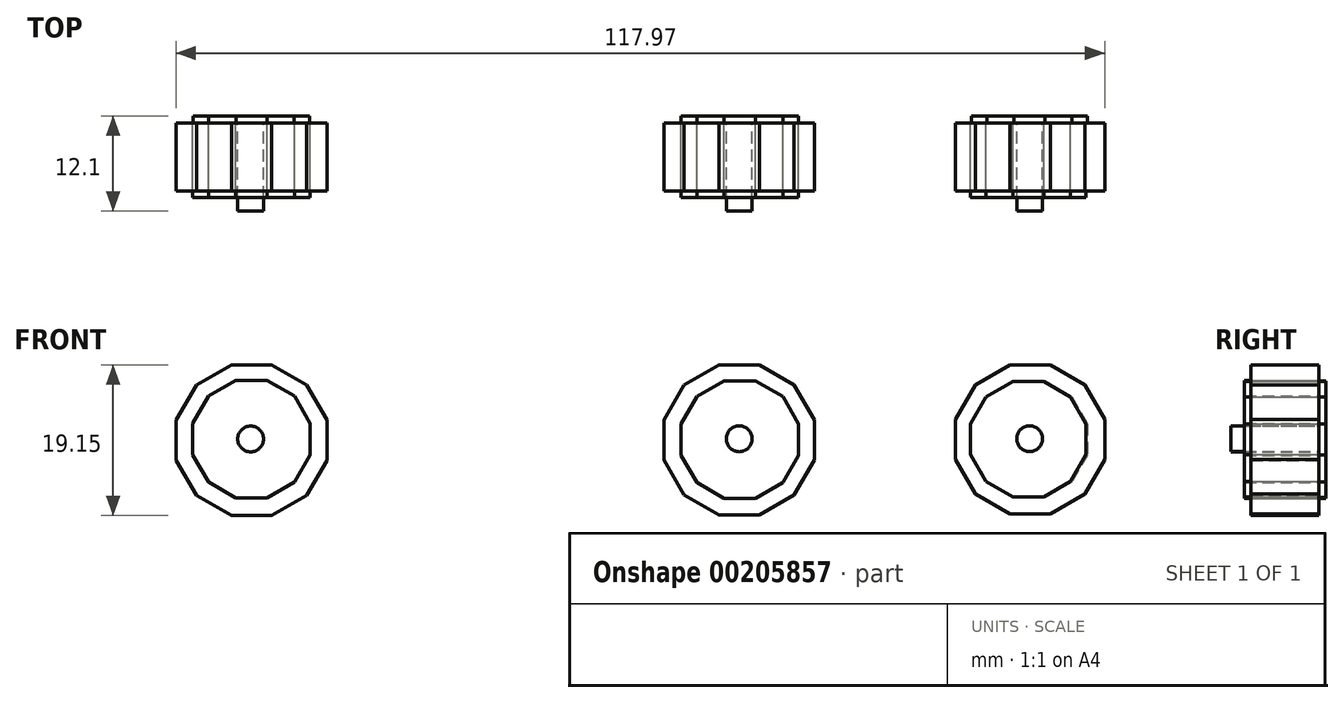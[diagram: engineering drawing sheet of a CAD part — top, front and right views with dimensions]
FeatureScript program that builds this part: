
annotation { "Feature Type Name" : "Feature", "Feature Type Description" : "" }
export const myFeature = defineFeature(function(context is Context, id is Id, definition is map)
    precondition{}
    {
        {
            var Q0;
            Q0=qCreatedBy(makeId("Front.planeOp"),FACE);
            cPlane(context, id + "F0", {"entities" : qUnion([Q0]), "cplaneType" : CPlaneType.OFFSET, "offset" : 20.32 * mm, "width" : 152.4 * mm, "height" : 152.4 * mm});
        }
        {
            var Q0;
            Q0=qCreatedBy(makeId("Front.planeOp"),FACE);
            cPlane(context, id + "F1", {"entities" : qUnion([Q0]), "cplaneType" : CPlaneType.OFFSET, "offset" : 10.16 * mm, "oppositeDirection" : true, "width" : 152.4 * mm, "height" : 152.4 * mm});
        }
        {
            var Q0;
            Q0=qCreatedBy(id+"F1.planeOp",FACE);
            var sketch = newSketch(context, id + "F2", { "sketchPlane" : qUnion([Q0])});
            skCircle(sketch, "E0.cCircle", {"center": v(54.19, -3.76) * mm, "radius": 9.48 * mm, "construction": true});
            skLineSegment(sketch, "E0.0", {"start": v(56.73, -13.25) * mm, "end": v(51.64, -13.25) * mm});
            skLineSegment(sketch, "E0.1", {"start": v(51.64, -13.25) * mm, "end": v(47.24, -10.7) * mm});
            skLineSegment(sketch, "E0.2", {"start": v(47.24, -10.7) * mm, "end": v(44.7, -6.3) * mm});
            skLineSegment(sketch, "E0.3", {"start": v(44.7, -6.3) * mm, "end": v(44.7, -1.22) * mm});
            skLineSegment(sketch, "E0.4", {"start": v(44.7, -1.22) * mm, "end": v(47.24, 3.18) * mm});
            skLineSegment(sketch, "E0.5", {"start": v(47.24, 3.18) * mm, "end": v(51.64, 5.72) * mm});
            skLineSegment(sketch, "E0.6", {"start": v(51.64, 5.72) * mm, "end": v(56.73, 5.72) * mm});
            skLineSegment(sketch, "E0.7", {"start": v(56.73, 5.72) * mm, "end": v(61.13, 3.18) * mm});
            skLineSegment(sketch, "E0.8", {"start": v(61.13, 3.18) * mm, "end": v(63.67, -1.22) * mm});
            skLineSegment(sketch, "E0.9", {"start": v(63.67, -1.22) * mm, "end": v(63.67, -6.3) * mm});
            skLineSegment(sketch, "E0.10", {"start": v(63.67, -6.3) * mm, "end": v(61.13, -10.7) * mm});
            skLineSegment(sketch, "E0.11", {"start": v(61.13, -10.7) * mm, "end": v(56.73, -13.25) * mm});
            skPoint(sketch, "E0.0.midPoint", {"position": v(54.19, -13.25) * mm});
            skCircle(sketch, "E1.cCircle", {"center": v(17.22, -3.82) * mm, "radius": 9.54 * mm, "construction": true});
            skLineSegment(sketch, "E1.0", {"start": v(14.67, 5.72) * mm, "end": v(19.78, 5.72) * mm});
            skLineSegment(sketch, "E1.1", {"start": v(19.78, 5.72) * mm, "end": v(24.21, 3.16) * mm});
            skLineSegment(sketch, "E1.2", {"start": v(24.21, 3.16) * mm, "end": v(26.77, -1.27) * mm});
            skLineSegment(sketch, "E1.3", {"start": v(26.77, -1.27) * mm, "end": v(26.77, -6.38) * mm});
            skLineSegment(sketch, "E1.4", {"start": v(26.77, -6.38) * mm, "end": v(24.21, -10.81) * mm});
            skLineSegment(sketch, "E1.5", {"start": v(24.21, -10.81) * mm, "end": v(19.78, -13.37) * mm});
            skLineSegment(sketch, "E1.6", {"start": v(19.78, -13.37) * mm, "end": v(14.67, -13.37) * mm});
            skLineSegment(sketch, "E1.7", {"start": v(14.67, -13.37) * mm, "end": v(10.24, -10.81) * mm});
            skLineSegment(sketch, "E1.8", {"start": v(10.24, -10.81) * mm, "end": v(7.68, -6.38) * mm});
            skLineSegment(sketch, "E1.9", {"start": v(7.68, -6.38) * mm, "end": v(7.68, -1.27) * mm});
            skLineSegment(sketch, "E1.10", {"start": v(7.68, -1.27) * mm, "end": v(10.24, 3.16) * mm});
            skLineSegment(sketch, "E1.11", {"start": v(10.24, 3.16) * mm, "end": v(14.67, 5.72) * mm});
            skPoint(sketch, "E1.0.midPoint", {"position": v(17.22, 5.72) * mm});
            skCircle(sketch, "E2.cCircle", {"center": v(-44.72, -3.86) * mm, "radius": 9.58 * mm, "construction": true});
            skLineSegment(sketch, "E2.0", {"start": v(-47.29, 5.72) * mm, "end": v(-42.15, 5.72) * mm});
            skLineSegment(sketch, "E2.1", {"start": v(-42.15, 5.72) * mm, "end": v(-37.7, 3.15) * mm});
            skLineSegment(sketch, "E2.2", {"start": v(-37.7, 3.15) * mm, "end": v(-35.14, -1.3) * mm});
            skLineSegment(sketch, "E2.3", {"start": v(-35.14, -1.3) * mm, "end": v(-35.14, -6.42) * mm});
            skLineSegment(sketch, "E2.4", {"start": v(-35.14, -6.42) * mm, "end": v(-37.7, -10.87) * mm});
            skLineSegment(sketch, "E2.5", {"start": v(-37.7, -10.87) * mm, "end": v(-42.15, -13.43) * mm});
            skLineSegment(sketch, "E2.6", {"start": v(-42.15, -13.43) * mm, "end": v(-47.29, -13.43) * mm});
            skLineSegment(sketch, "E2.7", {"start": v(-47.29, -13.43) * mm, "end": v(-51.73, -10.87) * mm});
            skLineSegment(sketch, "E2.8", {"start": v(-51.73, -10.87) * mm, "end": v(-54.3, -6.42) * mm});
            skLineSegment(sketch, "E2.9", {"start": v(-54.3, -6.42) * mm, "end": v(-54.3, -1.3) * mm});
            skLineSegment(sketch, "E2.10", {"start": v(-54.3, -1.3) * mm, "end": v(-51.73, 3.15) * mm});
            skLineSegment(sketch, "E2.11", {"start": v(-51.73, 3.15) * mm, "end": v(-47.29, 5.72) * mm});
            skPoint(sketch, "E2.0.midPoint", {"position": v(-44.72, 5.72) * mm});
            skSolve(sketch);
        }
        {
            var Q0;
            Q0=qCreatedBy(makeId("Top.planeOp"),FACE);
            cPlane(context, id + "F3", {"entities" : qUnion([Q0]), "cplaneType" : CPlaneType.OFFSET, "offset" : 19.8 * mm, "width" : 152.4 * mm, "height" : 152.4 * mm});
        }
        {
            var Q0;
            Q0=qCreatedBy(id+"F3.planeOp",FACE);
            cPlane(context, id + "F4", {"entities" : qUnion([Q0]), "cplaneType" : CPlaneType.OFFSET, "offset" : 10.16 * mm, "width" : 152.4 * mm, "height" : 152.4 * mm});
        }
        {
            var Q0;
            Q0=qCreatedBy(id+"F1.planeOp",FACE);
            var sketch = newSketch(context, id + "F5", { "sketchPlane" : qUnion([Q0])});
            skCircle(sketch, "E3.cCircle", {"center": v(-44.73, -3.73) * mm, "radius": 7.4 * mm, "construction": true});
            skLineSegment(sketch, "E3.0", {"start": v(-46.71, 3.67) * mm, "end": v(-42.75, 3.67) * mm});
            skLineSegment(sketch, "E3.1", {"start": v(-42.75, 3.67) * mm, "end": v(-39.3, 1.7) * mm});
            skLineSegment(sketch, "E3.2", {"start": v(-39.3, 1.7) * mm, "end": v(-37.33, -1.75) * mm});
            skLineSegment(sketch, "E3.3", {"start": v(-37.33, -1.75) * mm, "end": v(-37.33, -5.71) * mm});
            skLineSegment(sketch, "E3.4", {"start": v(-37.33, -5.71) * mm, "end": v(-39.3, -9.15) * mm});
            skLineSegment(sketch, "E3.5", {"start": v(-39.3, -9.15) * mm, "end": v(-42.75, -11.13) * mm});
            skLineSegment(sketch, "E3.6", {"start": v(-42.75, -11.13) * mm, "end": v(-46.71, -11.13) * mm});
            skLineSegment(sketch, "E3.7", {"start": v(-46.71, -11.13) * mm, "end": v(-50.15, -9.15) * mm});
            skLineSegment(sketch, "E3.8", {"start": v(-50.15, -9.15) * mm, "end": v(-52.13, -5.71) * mm});
            skLineSegment(sketch, "E3.9", {"start": v(-52.13, -5.71) * mm, "end": v(-52.13, -1.75) * mm});
            skLineSegment(sketch, "E3.10", {"start": v(-52.13, -1.75) * mm, "end": v(-50.15, 1.7) * mm});
            skLineSegment(sketch, "E3.11", {"start": v(-50.15, 1.7) * mm, "end": v(-46.71, 3.67) * mm});
            skPoint(sketch, "E3.0.midPoint", {"position": v(-44.73, 3.67) * mm});
            skCircle(sketch, "E4.cCircle", {"center": v(17.3, -3.81) * mm, "radius": 7.46 * mm, "construction": true});
            skLineSegment(sketch, "E4.0", {"start": v(15.3, 3.65) * mm, "end": v(19.3, 3.65) * mm});
            skLineSegment(sketch, "E4.1", {"start": v(19.3, 3.65) * mm, "end": v(22.76, 1.65) * mm});
            skLineSegment(sketch, "E4.2", {"start": v(22.76, 1.65) * mm, "end": v(24.76, -1.81) * mm});
            skLineSegment(sketch, "E4.3", {"start": v(24.76, -1.81) * mm, "end": v(24.76, -5.81) * mm});
            skLineSegment(sketch, "E4.4", {"start": v(24.76, -5.81) * mm, "end": v(22.76, -9.27) * mm});
            skLineSegment(sketch, "E4.5", {"start": v(22.76, -9.27) * mm, "end": v(19.3, -11.27) * mm});
            skLineSegment(sketch, "E4.6", {"start": v(19.3, -11.27) * mm, "end": v(15.3, -11.27) * mm});
            skLineSegment(sketch, "E4.7", {"start": v(15.3, -11.27) * mm, "end": v(11.84, -9.27) * mm});
            skLineSegment(sketch, "E4.8", {"start": v(11.84, -9.27) * mm, "end": v(9.84, -5.81) * mm});
            skLineSegment(sketch, "E4.9", {"start": v(9.84, -5.81) * mm, "end": v(9.84, -1.81) * mm});
            skLineSegment(sketch, "E4.10", {"start": v(9.84, -1.81) * mm, "end": v(11.84, 1.65) * mm});
            skLineSegment(sketch, "E4.11", {"start": v(11.84, 1.65) * mm, "end": v(15.3, 3.65) * mm});
            skPoint(sketch, "E4.0.midPoint", {"position": v(17.3, 3.65) * mm});
            skCircle(sketch, "E5.cCircle", {"center": v(54.1, -3.76) * mm, "radius": 7.35 * mm, "construction": true});
            skLineSegment(sketch, "E5.0", {"start": v(52.12, 3.59) * mm, "end": v(56.06, 3.59) * mm});
            skLineSegment(sketch, "E5.1", {"start": v(56.06, 3.59) * mm, "end": v(59.47, 1.62) * mm});
            skLineSegment(sketch, "E5.2", {"start": v(59.47, 1.62) * mm, "end": v(61.44, -1.79) * mm});
            skLineSegment(sketch, "E5.3", {"start": v(61.44, -1.79) * mm, "end": v(61.44, -5.73) * mm});
            skLineSegment(sketch, "E5.4", {"start": v(61.44, -5.73) * mm, "end": v(59.47, -9.14) * mm});
            skLineSegment(sketch, "E5.5", {"start": v(59.47, -9.14) * mm, "end": v(56.06, -11.1) * mm});
            skLineSegment(sketch, "E5.6", {"start": v(56.06, -11.1) * mm, "end": v(52.12, -11.1) * mm});
            skLineSegment(sketch, "E5.7", {"start": v(52.12, -11.1) * mm, "end": v(48.71, -9.14) * mm});
            skLineSegment(sketch, "E5.8", {"start": v(48.71, -9.14) * mm, "end": v(46.74, -5.73) * mm});
            skLineSegment(sketch, "E5.9", {"start": v(46.74, -5.73) * mm, "end": v(46.74, -1.79) * mm});
            skLineSegment(sketch, "E5.10", {"start": v(46.74, -1.79) * mm, "end": v(48.71, 1.62) * mm});
            skLineSegment(sketch, "E5.11", {"start": v(48.71, 1.62) * mm, "end": v(52.12, 3.59) * mm});
            skPoint(sketch, "E5.0.midPoint", {"position": v(54.1, 3.59) * mm});
            skSolve(sketch);
        }
        {
            var Q0;
            Q0=qCreatedBy(id+"F1.planeOp",FACE);
            var sketch = newSketch(context, id + "F6", { "sketchPlane" : qUnion([Q0])});
            skCircle(sketch, "E6.cCircle", {"center": v(53.94, -3.73) * mm, "radius": 7.34 * mm, "construction": true});
            skLineSegment(sketch, "E6.0", {"start": v(61.28, -1.77) * mm, "end": v(61.28, -5.7) * mm});
            skLineSegment(sketch, "E6.1", {"start": v(61.28, -5.7) * mm, "end": v(59.31, -9.1) * mm});
            skLineSegment(sketch, "E6.2", {"start": v(59.31, -9.1) * mm, "end": v(55.9, -11.07) * mm});
            skLineSegment(sketch, "E6.3", {"start": v(55.9, -11.07) * mm, "end": v(51.98, -11.07) * mm});
            skLineSegment(sketch, "E6.4", {"start": v(51.98, -11.07) * mm, "end": v(48.57, -9.1) * mm});
            skLineSegment(sketch, "E6.5", {"start": v(48.57, -9.1) * mm, "end": v(46.6, -5.7) * mm});
            skLineSegment(sketch, "E6.6", {"start": v(46.6, -5.7) * mm, "end": v(46.6, -1.77) * mm});
            skLineSegment(sketch, "E6.7", {"start": v(46.6, -1.77) * mm, "end": v(48.57, 1.64) * mm});
            skLineSegment(sketch, "E6.8", {"start": v(48.57, 1.64) * mm, "end": v(51.98, 3.6) * mm});
            skLineSegment(sketch, "E6.9", {"start": v(51.98, 3.6) * mm, "end": v(55.9, 3.6) * mm});
            skLineSegment(sketch, "E6.10", {"start": v(55.9, 3.6) * mm, "end": v(59.31, 1.64) * mm});
            skLineSegment(sketch, "E6.11", {"start": v(59.31, 1.64) * mm, "end": v(61.28, -1.77) * mm});
            skPoint(sketch, "E6.0.midPoint", {"position": v(61.28, -3.73) * mm});
            skCircle(sketch, "E7.cCircle", {"center": v(17.3, -3.78) * mm, "radius": 7.47 * mm, "construction": true});
            skLineSegment(sketch, "E7.0", {"start": v(9.83, -5.79) * mm, "end": v(9.83, -1.78) * mm});
            skLineSegment(sketch, "E7.1", {"start": v(9.83, -1.78) * mm, "end": v(11.83, 1.68) * mm});
            skLineSegment(sketch, "E7.2", {"start": v(11.83, 1.68) * mm, "end": v(15.3, 3.69) * mm});
            skLineSegment(sketch, "E7.3", {"start": v(15.3, 3.69) * mm, "end": v(19.3, 3.69) * mm});
            skLineSegment(sketch, "E7.4", {"start": v(19.3, 3.69) * mm, "end": v(22.77, 1.68) * mm});
            skLineSegment(sketch, "E7.5", {"start": v(22.77, 1.68) * mm, "end": v(24.77, -1.78) * mm});
            skLineSegment(sketch, "E7.6", {"start": v(24.77, -1.78) * mm, "end": v(24.77, -5.79) * mm});
            skLineSegment(sketch, "E7.7", {"start": v(24.77, -5.79) * mm, "end": v(22.77, -9.25) * mm});
            skLineSegment(sketch, "E7.8", {"start": v(22.77, -9.25) * mm, "end": v(19.3, -11.25) * mm});
            skLineSegment(sketch, "E7.9", {"start": v(19.3, -11.25) * mm, "end": v(15.3, -11.25) * mm});
            skLineSegment(sketch, "E7.10", {"start": v(15.3, -11.25) * mm, "end": v(11.83, -9.25) * mm});
            skLineSegment(sketch, "E7.11", {"start": v(11.83, -9.25) * mm, "end": v(9.83, -5.79) * mm});
            skPoint(sketch, "E7.0.midPoint", {"position": v(9.83, -3.78) * mm});
            skCircle(sketch, "E8.cCircle", {"center": v(-44.73, -3.72) * mm, "radius": 7.47 * mm, "construction": true});
            skLineSegment(sketch, "E8.0", {"start": v(-52.2, -5.72) * mm, "end": v(-52.2, -1.72) * mm});
            skLineSegment(sketch, "E8.1", {"start": v(-52.2, -1.72) * mm, "end": v(-50.2, 1.75) * mm});
            skLineSegment(sketch, "E8.2", {"start": v(-50.2, 1.75) * mm, "end": v(-46.73, 3.75) * mm});
            skLineSegment(sketch, "E8.3", {"start": v(-46.73, 3.75) * mm, "end": v(-42.73, 3.75) * mm});
            skLineSegment(sketch, "E8.4", {"start": v(-42.73, 3.75) * mm, "end": v(-39.26, 1.75) * mm});
            skLineSegment(sketch, "E8.5", {"start": v(-39.26, 1.75) * mm, "end": v(-37.26, -1.72) * mm});
            skLineSegment(sketch, "E8.6", {"start": v(-37.26, -1.72) * mm, "end": v(-37.26, -5.72) * mm});
            skLineSegment(sketch, "E8.7", {"start": v(-37.26, -5.72) * mm, "end": v(-39.26, -9.19) * mm});
            skLineSegment(sketch, "E8.8", {"start": v(-39.26, -9.19) * mm, "end": v(-42.73, -11.19) * mm});
            skLineSegment(sketch, "E8.9", {"start": v(-42.73, -11.19) * mm, "end": v(-46.73, -11.19) * mm});
            skLineSegment(sketch, "E8.10", {"start": v(-46.73, -11.19) * mm, "end": v(-50.2, -9.19) * mm});
            skLineSegment(sketch, "E8.11", {"start": v(-50.2, -9.19) * mm, "end": v(-52.2, -5.72) * mm});
            skPoint(sketch, "E8.0.midPoint", {"position": v(-52.2, -3.72) * mm});
            skSolve(sketch);
        }
        {
            var Q0;
            Q0 = qSketchRegion(id + "F2", true);
            extrude(context, id + "F7", {"entities" : qUnion([Q0]), "depth" : 8.64 * mm});
        }
        {
            var Q0;
            Q0 = qSketchRegion(id + "F5", true);
            extrude(context, id + "F8", {"entities" : qUnion([Q0]), "oppositeDirection" : true, "depth" : 0.92 * mm});
        }
        {
            var Q0;
            Q0 = qSketchRegion(id + "F6", true);
            extrude(context, id + "F9", {"entities" : qUnion([Q0]), "depth" : 9.45 * mm});
        }
        {
            var Q0;
            Q0=qCreatedBy(id+"F1.planeOp",FACE);
            var sketch = newSketch(context, id + "F10", { "sketchPlane" : qUnion([Q0])});
            skCircle(sketch, "E9", {"center": v(-44.83, -3.7) * mm, "radius": 1.64 * mm});
            skCircle(sketch, "E10", {"center": v(54.1, -3.67) * mm, "radius": 1.64 * mm});
            skCircle(sketch, "E11", {"center": v(17.22, -3.7) * mm, "radius": 1.64 * mm});
            skSolve(sketch);
        }
        {
            var Q0;
            Q0 = qSketchRegion(id + "F10", true);
            extrude(context, id + "F11", {"entities" : qUnion([Q0]), "depth" : 11.18 * mm});
        }
    });
